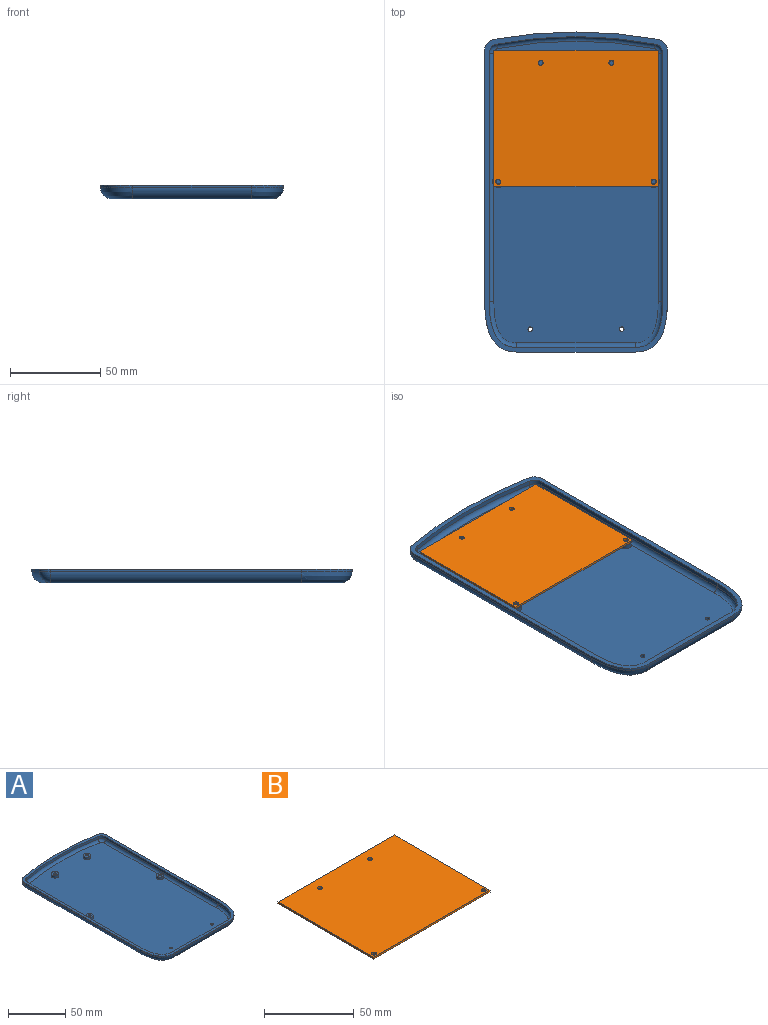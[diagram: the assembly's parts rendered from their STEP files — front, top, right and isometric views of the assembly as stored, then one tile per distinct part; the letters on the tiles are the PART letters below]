
ASSEMBLY  parts=2 mates=1
PART A: 53 faces, bbox 101.6x181.9x10.9 mm
  f0: plane 167.64x91.44mm, normal (0,0,1), area 14958.9mm2, adj f6,f10,f14,f18,f31,f32,f33,f34
  f1: plane 165.1x88.9mm, normal (0,0,-1), area 14471.5mm2, adj f38,f40,f41,f43,f45,f46,f47,f48
  f2: plane 139.53x1.27mm, normal (1,0,0), area 177.2mm2, adj f28,f30,f37,f38
  f3: plane 66.04x1.27mm, normal (0,-1,0), area 83.9mm2, adj f27,f28,f30,f43
  f4: plane 139.53x1.27mm, normal (-1,0,0), area 177.2mm2, adj f27,f30,f42,f46
  f5: cylinder r=1.27mm len=2.54mm, axis (0,0,-1), area 20.3mm2, adj f7,f8
  f6: cylinder r=3.17mm len=6.35mm, axis (0,0,-1), area 50.7mm2, adj f0,f7,f36
  f7: plane 6.35x6.35mm, normal (0,0,1), area 26.6mm2, adj f5,f6
  f8: plane 2.54x2.54mm, normal (0,0,1), area 5.1mm2, adj f5
  f9: cylinder r=1.27mm len=2.54mm, axis (0,0,-1), area 20.3mm2, adj f11,f12
  f10: cylinder r=3.17mm len=6.35mm, axis (0,0,-1), area 50.7mm2, adj f0,f11,f32
  f11: plane 6.35x6.35mm, normal (0,0,1), area 26.6mm2, adj f9,f10
  f12: plane 2.54x2.54mm, normal (0,0,1), area 5.1mm2, adj f9
  f13: cylinder r=1.27mm len=2.54mm, axis (0,0,-1), area 20.3mm2, adj f15,f16
  f14: cylinder r=3.17mm len=6.35mm, axis (0,0,-1), area 50.7mm2, adj f0,f15
  f15: plane 6.35x6.35mm, normal (0,0,1), area 26.6mm2, adj f13,f14
  f16: plane 2.54x2.54mm, normal (0,0,1), area 5.1mm2, adj f13
  f17: cylinder r=1.27mm len=2.54mm, axis (0,0,-1), area 20.3mm2, adj f19,f20
  f18: cylinder r=3.17mm len=6.35mm, axis (0,0,-1), area 50.7mm2, adj f0,f19
  f19: plane 6.35x6.35mm, normal (0,0,1), area 26.6mm2, adj f17,f18
  f20: plane 2.54x2.54mm, normal (0,0,1), area 5.1mm2, adj f17
  f21: plane 138.09x2.54mm, normal (-1,0,0), area 350.7mm2, adj f22,f30,f32,f51
  f22: extruded ~25.4x15.24mm, area 84.8mm2, adj f21,f23,f30,f31
  f23: plane 66.04x2.54mm, normal (0,1,0), area 167.7mm2, adj f22,f24,f30,f33
  f24: extruded ~25.4x15.24mm, area 84.8mm2, adj f23,f25,f30,f35
  f25: plane 138.09x2.54mm, normal (1,0,0), area 350.7mm2, adj f24,f30,f36,f49
  f26: cylinder r=256.54mm len=91.16mm, axis (0,0,-1), area 116.4mm2, adj f30,f37,f41,f42
  f27: extruded ~27.94x17.78mm, area 47.6mm2, adj f3,f4,f30,f45
  f28: extruded ~27.94x17.78mm, area 47.6mm2, adj f2,f3,f30,f40
  f29: cylinder r=231.78mm len=88.3mm, axis (0,0,-1), area 225.6mm2, adj f30,f34,f49,f51
  f30: plane 177.8x101.6mm, normal (0,0,1), area 1344.2mm2, adj f2,f3,f4,f21,f22,f23,f24,f25
  f31: bspline ~35.21x24.74mm, area 127.4mm2, adj f0,f22,f32,f33
  f32: cylinder r=2.54mm len=138.09mm, axis (0,-1,0), area 549.3mm2, adj f0,f10,f21,f31,f52
  f33: cylinder r=2.54mm len=66.04mm, axis (-1,0,0), area 263.5mm2, adj f0,f23,f31,f35
  f34: torus R=229.23mm, axis (0,0,1), area 353mm2, adj f0,f29,f50,f52
  f35: bspline ~27.89x24.74mm, area 127.4mm2, adj f0,f24,f33,f36
  f36: cylinder r=2.54mm len=138.09mm, axis (0,1,0), area 549.3mm2, adj f0,f6,f25,f35,f50
  f37: cylinder r=6.35mm len=6.25mm, axis (0,0,-1), area 11.2mm2, adj f2,f26,f30,f39
  f38: cylinder r=6.35mm len=139.53mm, axis (0,1,0), area 1391.7mm2, adj f1,f2,f39,f40
  f39: sphere r=6.35mm, area 56.1mm2, adj f37,f38,f41
  f40: bspline ~38.77x28.63mm, area 337.6mm2, adj f1,f28,f38,f43
  f41: torus R=250.19mm, axis (0,0,1), area 905.9mm2, adj f1,f26,f39,f44
  f42: cylinder r=6.35mm len=6.25mm, axis (0,0,-1), area 11.2mm2, adj f4,f26,f30,f44
  f43: cylinder r=6.35mm len=66.04mm, axis (1,0,0), area 658.7mm2, adj f1,f3,f40,f45
  f44: sphere r=6.35mm, area 56.1mm2, adj f41,f42,f46
  f45: bspline ~38.77x28.63mm, area 337.6mm2, adj f1,f27,f43,f46
  f46: cylinder r=6.35mm len=139.53mm, axis (0,-1,0), area 1391.7mm2, adj f1,f4,f44,f45
  f47: cylinder r=1.27mm len=2.54mm, axis (0,0,-1), area 20.3mm2, adj f0,f1
  f48: cylinder r=1.27mm len=2.54mm, axis (0,0,-1), area 20.3mm2, adj f0,f1
  f49: cylinder r=5.08mm len=4.99mm, axis (0,0,-1), area 17.8mm2, adj f25,f29,f30,f50
  f50: torus R=2.54mm, axis (0,0,1), area 22.9mm2, adj f0,f34,f36,f49
  f51: cylinder r=5.08mm len=4.99mm, axis (0,0,-1), area 17.8mm2, adj f21,f29,f30,f52
  f52: torus R=2.54mm, axis (0,0,1), area 22.9mm2, adj f0,f32,f34,f51
PART B: 10 faces, bbox 91.4x75.6x1.2 mm
  f0: plane 91.44x1.2mm, normal (0,1,0), area 109.7mm2, adj f1,f3,f4,f5
  f1: plane 75.57x1.2mm, normal (-1,0,0), area 90.7mm2, adj f0,f2,f4,f5
  f2: plane 91.44x1.2mm, normal (0,-1,0), area 109.7mm2, adj f1,f3,f4,f5
  f3: plane 75.57x1.2mm, normal (1,0,0), area 90.7mm2, adj f0,f2,f4,f5
  f4: plane 91.44x75.57mm, normal (0,0,1), area 6885.1mm2, adj f0,f1,f2,f3,f6,f7,f8,f9
  f5: plane 91.44x75.57mm, normal (0,0,-1), area 6885.1mm2, adj f0,f1,f2,f3,f6,f7,f8,f9
  f6: cylinder r=1.4mm len=2.79mm, axis (0,0,1), area 10.5mm2, adj f4,f5
  f7: cylinder r=1.4mm len=2.79mm, axis (0,0,1), area 10.5mm2, adj f4,f5
  f8: cylinder r=1.4mm len=2.79mm, axis (0,0,1), area 10.5mm2, adj f4,f5
  f9: cylinder r=1.4mm len=2.79mm, axis (0,0,1), area 10.5mm2, adj f4,f5
PLACE A t=(-34.95,-21.19,-14.96)mm
PLACE B t=(-80.67,57.55,-9.88)mm
MATE fastened B.f9 <-> A.f5  axis (0,0,-1) through (-78.13,-15.48,-9.88)mm
